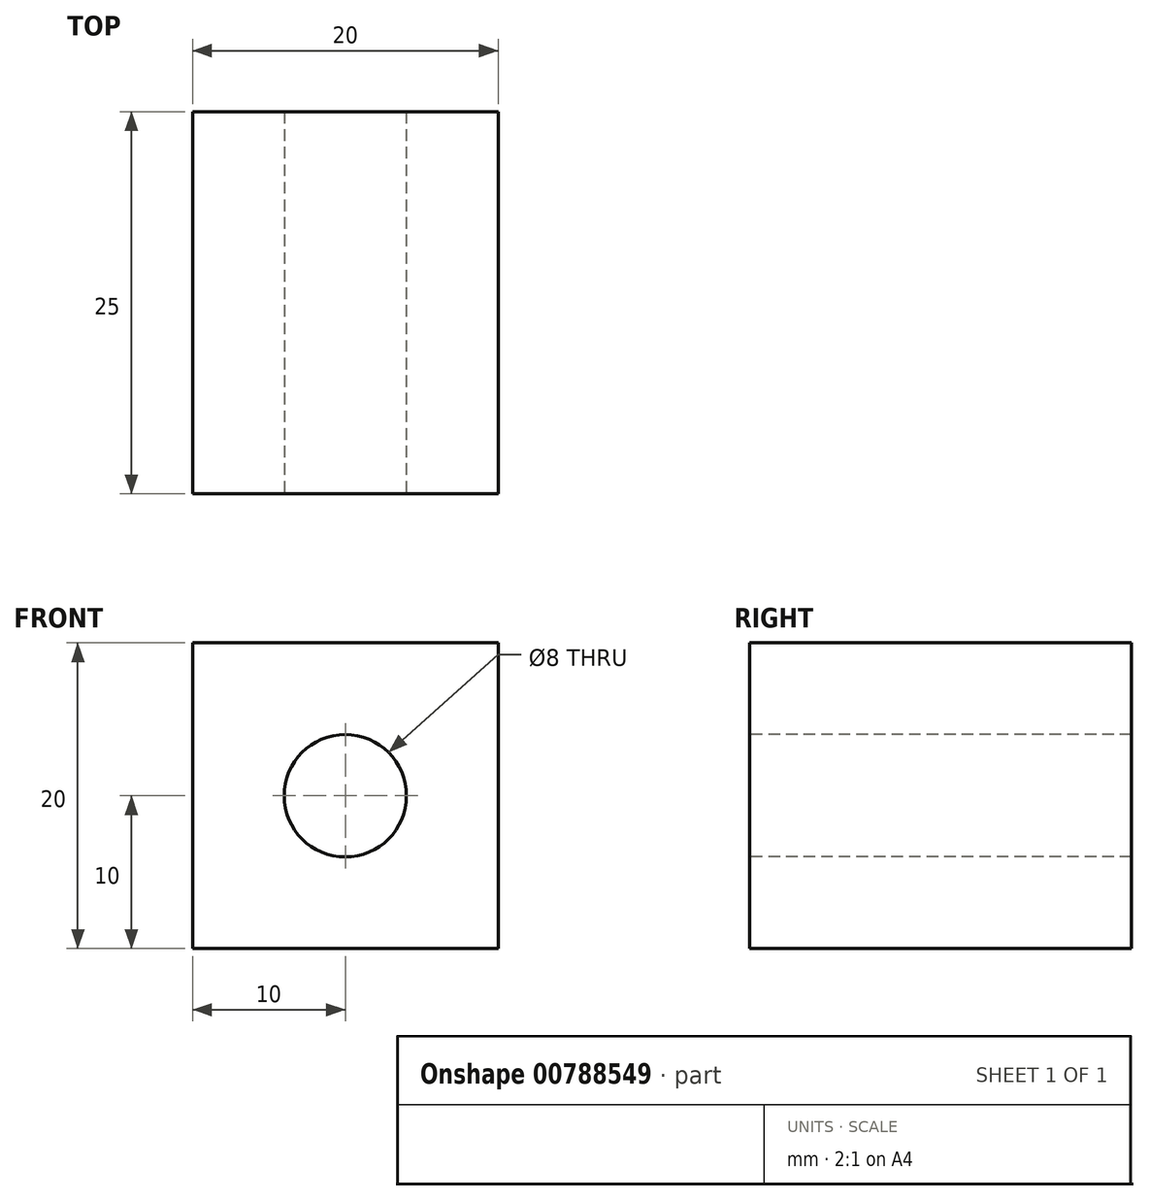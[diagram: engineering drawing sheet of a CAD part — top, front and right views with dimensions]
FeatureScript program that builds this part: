
annotation { "Feature Type Name" : "Feature", "Feature Type Description" : "" }
export const myFeature = defineFeature(function(context is Context, id is Id, definition is map)
    precondition{}
    {
        {
            var Q0;
            Q0=qCreatedBy(makeId("Front.planeOp"),FACE);
            var sketch = newSketch(context, id + "F0", { "sketchPlane" : qUnion([Q0])});
            skLineSegment(sketch, "E0.bottom", {"start": v(10, 10) * mm, "end": v(-10, 10) * mm});
            skLineSegment(sketch, "E0.top", {"start": v(10, -10) * mm, "end": v(-10, -10) * mm});
            skLineSegment(sketch, "E0.left", {"start": v(10, 10) * mm, "end": v(10, -10) * mm});
            skLineSegment(sketch, "E0.right", {"start": v(-10, 10) * mm, "end": v(-10, -10) * mm});
            skPoint(sketch, "E0.middle", {"position": v(0, 0) * mm});
            skSolve(sketch);
        }
        {
            var Q0;
            Q0=makeQuery(id+"F0.imprint","IMPRINT",FACE,{"disambiguationData":[TD([[makeQuery(id+"F0.imprint","IMPRINT",EDGE,{"derivedFrom":sQuery(id+"F0.wireOp",EDGE,"E0.bottom")}),1.0]])]});
            extrude(context, id + "F1", {"entities" : qUnion([Q0]), "endBound" : BoundingType.SYMMETRIC, "oppositeDirection" : true, "depth" : 25 * mm, "offsetDistance" : 25 * mm});
        }
        {
            var Q0;
            Q0=makeQuery(id+"F1.opExtrude","CAP_FACE",FACE,{"disambiguationData":[OSD([sQuery(id+"F0.wireOp",EDGE,"E0.bottom"),sQuery(id+"F0.wireOp",EDGE,"E0.top"),sQuery(id+"F0.wireOp",EDGE,"E0.left"),sQuery(id+"F0.wireOp",EDGE,"E0.right")])],"isStart":true});
            var sketch = newSketch(context, id + "F2", { "sketchPlane" : qUnion([Q0])});
            skCircle(sketch, "E1", {"center": v(0, 0) * mm, "radius": 4 * mm});
            skSolve(sketch);
        }
        {
            var Q0;
            Q0=makeQuery(id+"F2.imprint","IMPRINT",FACE,{"disambiguationData":[TD([[makeQuery(id+"F2.imprint","IMPRINT",EDGE,{"derivedFrom":sQuery(id+"F2.wireOp",EDGE,"E1")}),1.0]])]});
            extrude(context, id + "F3", {"entities" : qUnion([Q0]), "operationType" : NewBodyOperationType.REMOVE, "oppositeDirection" : true, "depth" : 30 * mm, "offsetDistance" : 25 * mm});
        }
    });
